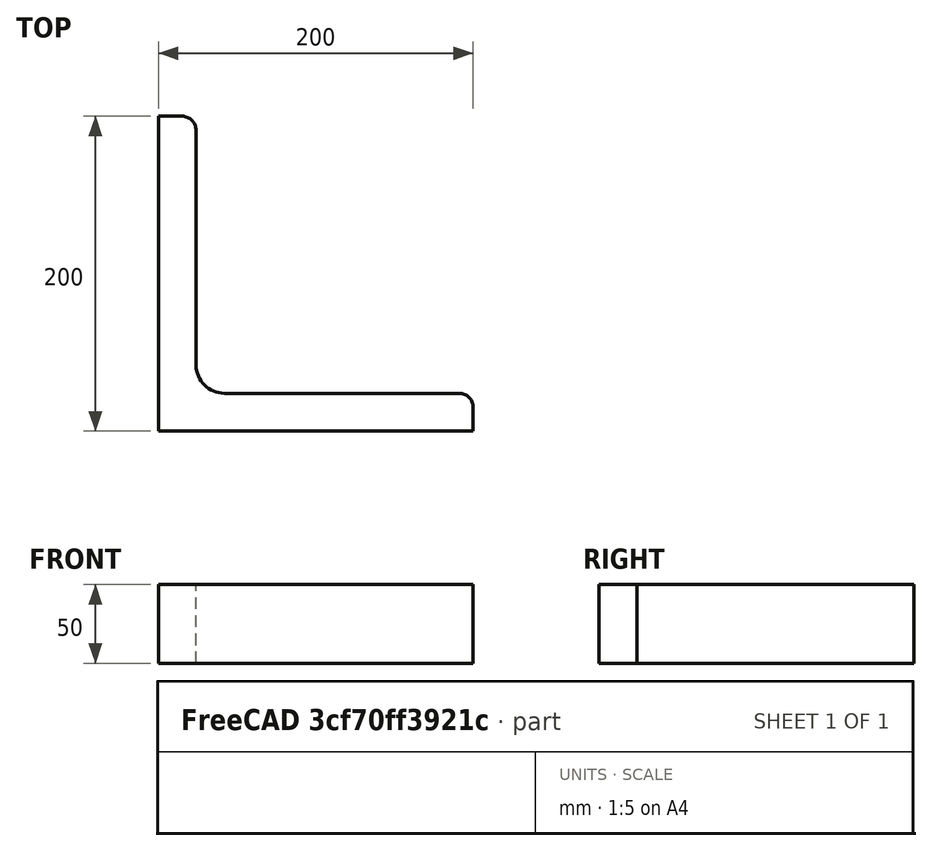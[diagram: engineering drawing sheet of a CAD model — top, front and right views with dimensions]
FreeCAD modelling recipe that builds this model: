
FCSTD DOCUMENT  (FreeCAD 0.15R4671 (Git))
Label: Angle Bar L200x200x24 EN10056 S235JR
License: All rights reserved
LicenseURL: http://en.wikipedia.org/wiki/All_rights_reserved
objects: Sketcher::SketchObject×1, Part::Extrusion×1
note: 2 computed .brp shape members not serialized (recipe doc carries the construction recipe); baked Part::Feature solids carry a one-line shape summary decoded from their .brp

FEATURE [Sketcher::SketchObject] Sketch
  sketch-geometry (9):
    g0: LineSegment StartX=0 StartY=0 StartZ=0 EndX=200 EndY=0 EndZ=0
    g1: LineSegment StartX=200 StartY=0 StartZ=0 EndX=200 EndY=15 EndZ=0
    g2: LineSegment StartX=191 StartY=24 StartZ=0 EndX=42 EndY=24 EndZ=0
    g3: LineSegment StartX=0 StartY=0 StartZ=0 EndX=0 EndY=200 EndZ=0
    g4: LineSegment StartX=0 StartY=200 StartZ=0 EndX=15 EndY=200 EndZ=0
    g5: LineSegment StartX=24 StartY=191 StartZ=0 EndX=24 EndY=42 EndZ=0
    g6: ArcOfCircle CenterX=42 CenterY=42 CenterZ=0 NormalX=0 NormalY=0 NormalZ=1 Radius=18 StartAngle=3.14159 EndAngle=4.71239
    g7: ArcOfCircle CenterX=15 CenterY=191 CenterZ=0 NormalX=0 NormalY=0 NormalZ=1 Radius=9 StartAngle=0 EndAngle=1.5708
    g8: ArcOfCircle CenterX=191 CenterY=15 CenterZ=0 NormalX=0 NormalY=0 NormalZ=1 Radius=9 StartAngle=0 EndAngle=1.5708
  constraints (23):
    c: Coincident(g0,g-1)
    c: Horizontal(g0)
    c: Coincident(g1,g0)
    c: Vertical(g1)
    c: Horizontal(g2)
    c: Coincident(g3,g-1)
    c: Vertical(g3)
    c: Coincident(g4,g3)
    c: Horizontal(g4)
    c: Vertical(g5)
    c: Tangent(g5,g6) = -1.5708
    c: Tangent(g2,g6) = 1.5708
    c: Tangent(g4,g7) = 1.5708
    c: Tangent(g5,g7) = 1.5708
    c: Tangent(g2,g8) = -1.5708
    c: Tangent(g1,g8) = -1.5708
    c: DistanceX(g0) = 200
    c: DistanceY(g3) = 200
    c: DistanceY(g0,g2) = 24
    c: DistanceX(g3,g5) = 24
    c: Radius(g6) = 18
    c: Radius(g8) = 9
    c: Radius(g7) = 9
FEATURE [Part::Extrusion] Extrude  label="Angle Bar L200x200x24 EN10056 S235JR"
  Base = -> Sketch
  Dir = (0,0,50)
  Solid = true
